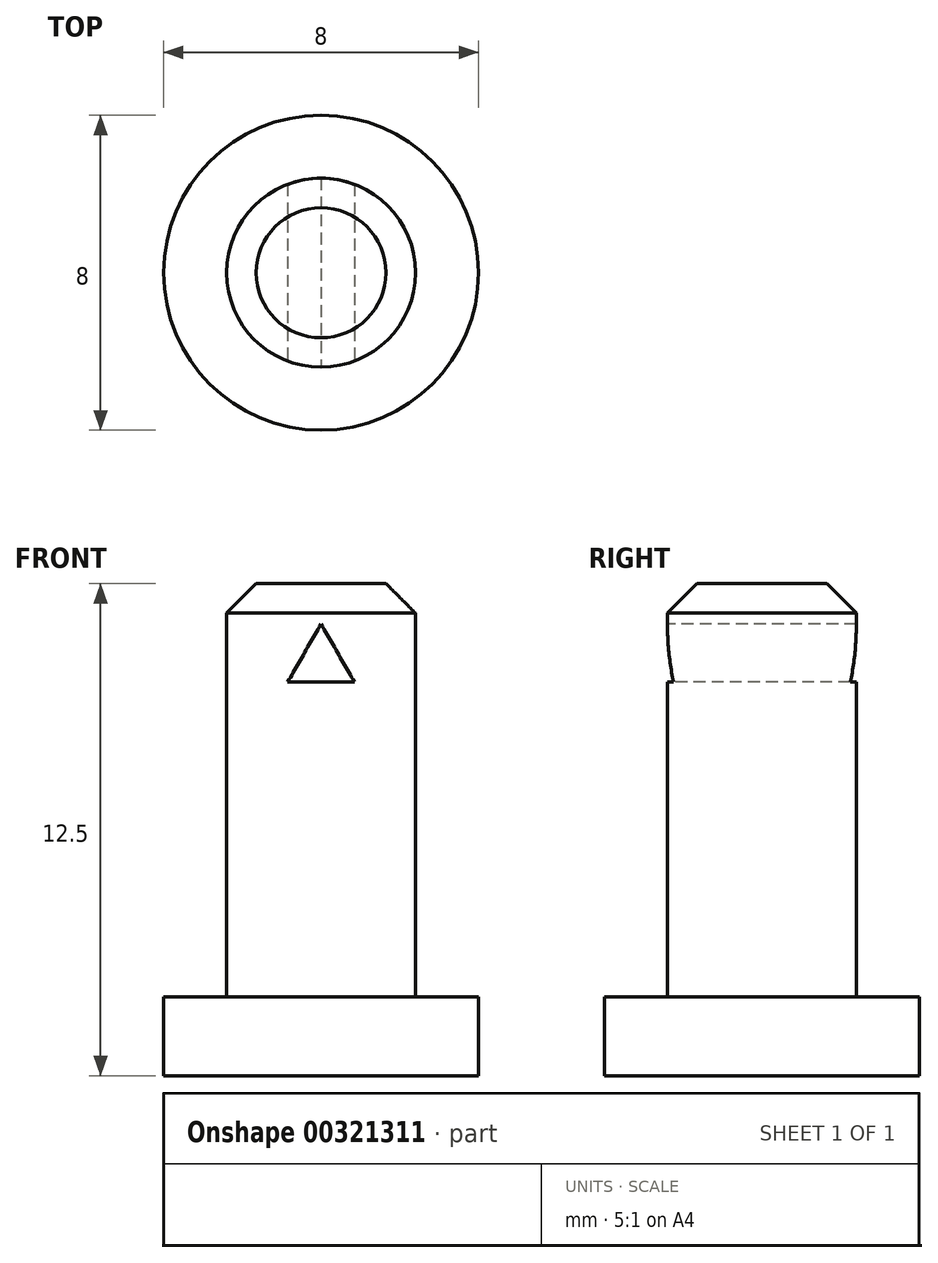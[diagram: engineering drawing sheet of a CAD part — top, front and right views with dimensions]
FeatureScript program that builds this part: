
annotation { "Feature Type Name" : "Feature", "Feature Type Description" : "" }
export const myFeature = defineFeature(function(context is Context, id is Id, definition is map)
    precondition{}
    {
        {
            var Q0;
            Q0=qCreatedBy(makeId("Top.planeOp"),FACE);
            var sketch = newSketch(context, id + "F0", { "sketchPlane" : qUnion([Q0])});
            skCircle(sketch, "E0", {"center": v(0, 0) * mm, "radius": 4 * mm});
            skSolve(sketch);
        }
        {
            var Q0;
            Q0 = qSketchRegion(id + "F0", true);
            extrude(context, id + "F1", {"entities" : qUnion([Q0]), "depth" : 2 * mm});
        }
        {
            var Q0;
            Q0=makeQuery(id+"F1.opExtrude","CAP_FACE",FACE,{"disambiguationData":[OSD([sQuery(id+"F0.wireOp",EDGE,"E0")])],"isStart":false});
            var sketch = newSketch(context, id + "F2", { "sketchPlane" : qUnion([Q0])});
            skCircle(sketch, "E1", {"center": v(0, 0) * mm, "radius": 2.4 * mm});
            skSolve(sketch);
        }
        {
            var Q0;
            Q0 = qSketchRegion(id + "F2", true);
            extrude(context, id + "F3", {"entities" : qUnion([Q0]), "operationType" : NewBodyOperationType.ADD, "depth" : 10.5 * mm});
        }
        {
            var Q0;
            Q0=qCreatedBy(makeId("Front.planeOp"),FACE);
            var sketch = newSketch(context, id + "F4", { "sketchPlane" : qUnion([Q0])});
            skLineSegment(sketch, "E2", {"start": v(-0.85, 10) * mm, "end": v(0.85, 10) * mm});
            skLineSegment(sketch, "E3", {"start": v(0.85, 10) * mm, "end": v(0, 11.47) * mm});
            skLineSegment(sketch, "E4", {"start": v(0, 11.47) * mm, "end": v(-0.85, 10) * mm});
            skSolve(sketch);
        }
        {
            var Q0;
            Q0 = qSketchRegion(id + "F4", true);
            extrude(context, id + "F5", {"entities" : qUnion([Q0]), "operationType" : NewBodyOperationType.REMOVE, "endBound" : BoundingType.SYMMETRIC, "oppositeDirection" : true, "depth" : 10 * mm});
        }
        {
            var Q0;
            Q0=makeQuery(id+"F3.opExtrude","CAP_EDGE",EDGE,{"disambiguationData":[OSD([sQuery(id+"F2.wireOp",EDGE,"E1")])],"isStart":false});
            chamfer(context, id + "F6", {"entities" : qUnion([Q0]), "width" : 0.75 * mm, "tangentPropagation" : true});
        }
    });
